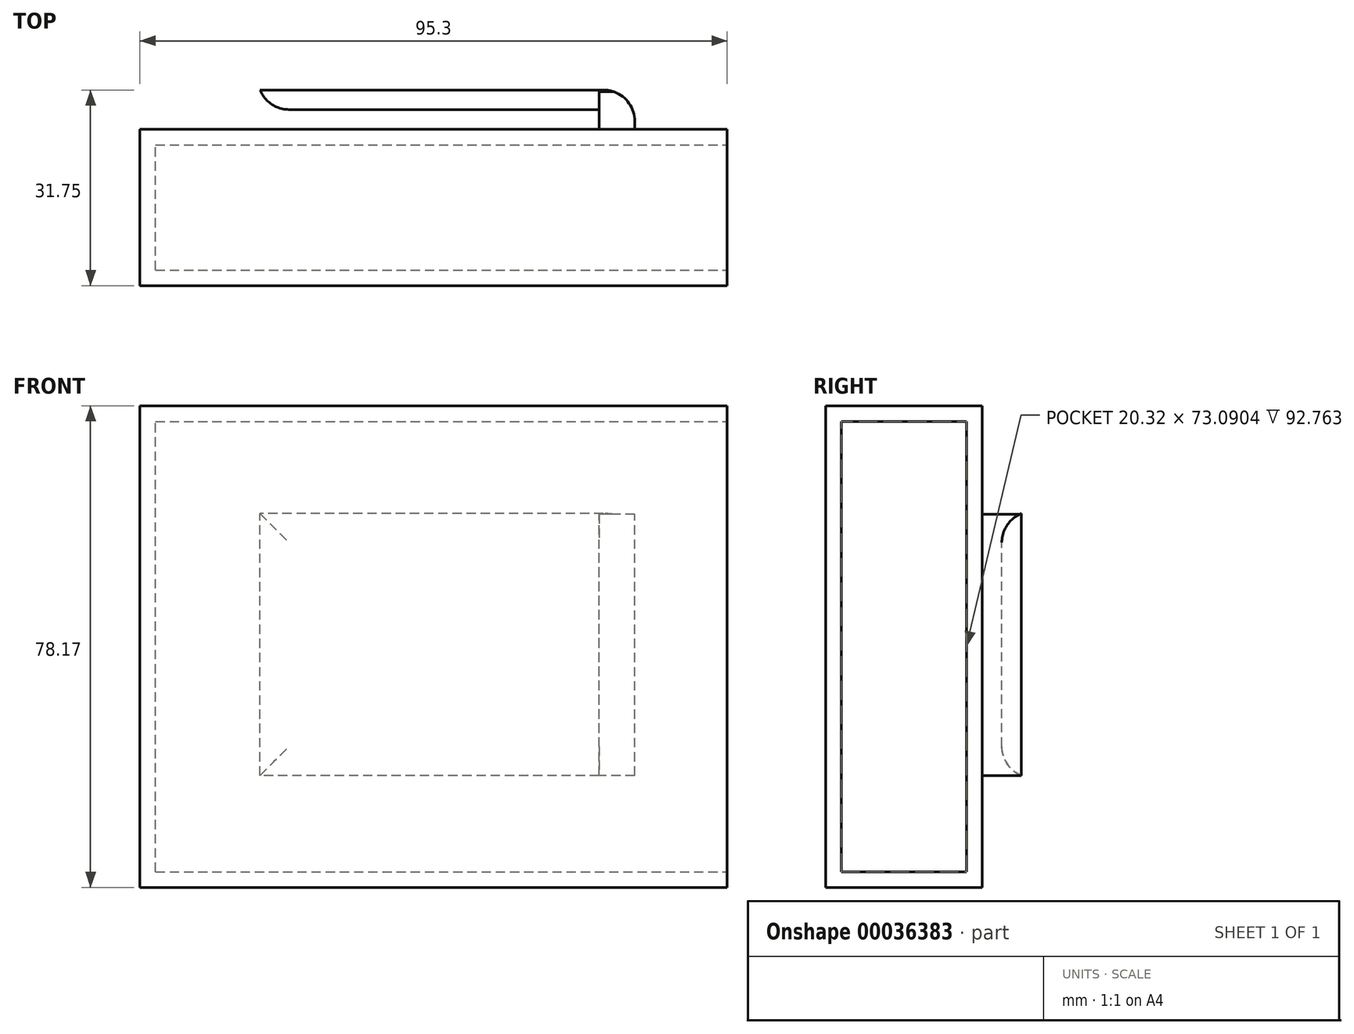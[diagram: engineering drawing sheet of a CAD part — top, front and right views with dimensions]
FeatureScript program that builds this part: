
annotation { "Feature Type Name" : "Feature", "Feature Type Description" : "" }
export const myFeature = defineFeature(function(context is Context, id is Id, definition is map)
    precondition{}
    {
        {
            var Q0;
            Q0=qCreatedBy(makeId("Front.planeOp"),FACE);
            var sketch = newSketch(context, id + "F0", { "sketchPlane" : qUnion([Q0])});
            skLineSegment(sketch, "E0.bottom", {"start": v(0, 0) * mm, "end": v(95.3, 0) * mm});
            skLineSegment(sketch, "E0.top", {"start": v(0, 78.17) * mm, "end": v(95.3, 78.17) * mm});
            skLineSegment(sketch, "E0.left", {"start": v(0, 0) * mm, "end": v(0, 78.17) * mm});
            skLineSegment(sketch, "E0.right", {"start": v(95.3, 0) * mm, "end": v(95.3, 78.17) * mm});
            skSolve(sketch);
        }
        {
            var Q0;
            Q0=makeQuery(id+"F0.imprint","IMPRINT",FACE,{"disambiguationData":[TD([[makeQuery(id+"F0.imprint","IMPRINT",EDGE,{"derivedFrom":sQuery(id+"F0.wireOp",EDGE,"E0.bottom")}),1.0]])]});
            extrude(context, id + "F1", {"entities" : qUnion([Q0]), "depth" : 25.4 * mm});
        }
        {
            var Q0;
            Q0=makeQuery(id+"F1.opExtrude","SWEPT_FACE",FACE,{"disambiguationData":[OSD([sQuery(id+"F0.wireOp",EDGE,"E0.right")])]});
            shell(context, id + "F2", {"entities" : qUnion([Q0]), "thickness" : 2.54 * mm});
        }
        {
            var Q0;
            Q0=makeQuery(id+"F1.opExtrude","CAP_FACE",FACE,{"disambiguationData":[OSD([sQuery(id+"F0.wireOp",EDGE,"E0.bottom"),sQuery(id+"F0.wireOp",EDGE,"E0.top"),sQuery(id+"F0.wireOp",EDGE,"E0.left"),sQuery(id+"F0.wireOp",EDGE,"E0.right")])],"isStart":true});
            var sketch = newSketch(context, id + "F3", { "sketchPlane" : qUnion([Q0])});
            skLineSegment(sketch, "E1.bottom", {"start": v(-80.29, 18.15) * mm, "end": v(-74.51, 18.15) * mm});
            skLineSegment(sketch, "E1.top", {"start": v(-80.29, 60.54) * mm, "end": v(-74.51, 60.54) * mm});
            skLineSegment(sketch, "E1.left", {"start": v(-80.29, 18.15) * mm, "end": v(-80.29, 60.54) * mm});
            skLineSegment(sketch, "E1.right", {"start": v(-74.51, 18.15) * mm, "end": v(-74.51, 60.54) * mm});
            skSolve(sketch);
        }
        {
            var Q0;
            Q0=makeQuery(id+"F3.imprint","IMPRINT",FACE,{"disambiguationData":[TD([[makeQuery(id+"F3.imprint","IMPRINT",EDGE,{"derivedFrom":sQuery(id+"F3.wireOp",EDGE,"E1.bottom")}),1.0]])]});
            extrude(context, id + "F4", {"entities" : qUnion([Q0]), "operationType" : NewBodyOperationType.ADD, "depth" : 3.17 * mm});
        }
        {
            var Q0;
            Q0=makeQuery(id+"F4.opExtrude","CAP_FACE",FACE,{"disambiguationData":[OSD([sQuery(id+"F3.wireOp",EDGE,"E1.bottom"),sQuery(id+"F3.wireOp",EDGE,"E1.top"),sQuery(id+"F3.wireOp",EDGE,"E1.left"),sQuery(id+"F3.wireOp",EDGE,"E1.right")])],"isStart":false});
            var sketch = newSketch(context, id + "F5", { "sketchPlane" : qUnion([Q0])});
            skLineSegment(sketch, "E2.bottom", {"start": v(-80.29, 18.15) * mm, "end": v(-19.47, 18.15) * mm});
            skLineSegment(sketch, "E2.top", {"start": v(-80.29, 60.67) * mm, "end": v(-19.47, 60.67) * mm});
            skLineSegment(sketch, "E2.left", {"start": v(-80.29, 18.15) * mm, "end": v(-80.29, 60.67) * mm});
            skLineSegment(sketch, "E2.right", {"start": v(-19.47, 18.15) * mm, "end": v(-19.47, 60.67) * mm});
            skSolve(sketch);
        }
        {
            var Q0;
            {var subQ4=sQuery(id+"F5.wireOp",EDGE,"E2.top");Q0=makeQuery(id+"F5.imprint","IMPRINT",FACE,{"disambiguationData":[TD([[makeQuery(id+"F5.imprint","IMPRINT",EDGE,{"derivedFrom":subQ4}),-1.0]])]});}
            var Q1;
            {var subQ1=makeQuery(id+"F4.opExtrude","CAP_EDGE",EDGE,{"disambiguationData":[OSD([sQuery(id+"F3.wireOp",EDGE,"E1.top")])],"isStart":false});Q1=makeQuery(id+"F5.imprint","IMPRINT",FACE,{"disambiguationData":[TD([[makeQuery(id+"F5.imprint","IMPRINT",EDGE,{"derivedFrom":subQ1}),-1.0]])]});}
            extrude(context, id + "F6", {"entities" : qUnion([Q0, Q1]), "operationType" : NewBodyOperationType.ADD, "depth" : 3.17 * mm});
        }
        {
            var Q0;
            Q0=makeQuery(id+"F6.opExtrude","CAP_EDGE",EDGE,{"disambiguationData":[OSD([sQuery(id+"F5.wireOp",EDGE,"E2.right")])],"isStart":true});
            var Q1;
            Q1=makeQuery(id+"F6.opExtrude","CAP_EDGE",EDGE,{"disambiguationData":[OSD([sQuery(id+"F5.wireOp",EDGE,"E2.top")])],"isStart":true});
            var Q2;
            Q2=makeQuery(id+"F6.opExtrude","CAP_EDGE",EDGE,{"disambiguationData":[OSD([sQuery(id+"F5.wireOp",EDGE,"E2.bottom")])],"isStart":true});
            fillet(context, id + "F7", {"entities" : qUnion([Q0, Q1, Q2]), "radius" : 5.08 * mm, "tangentPropagation" : true, "allowEdgeOverflow" : false});
        }
        {
            var Q0;
            Q0=makeQuery(id+"F4.opExtrude","CAP_EDGE",EDGE,{"disambiguationData":[OSD([sQuery(id+"F3.wireOp",EDGE,"E1.right")])],"isStart":false});
            var Q1;
            Q1=makeQuery(id+"F6.opExtrude","CAP_EDGE",EDGE,{"disambiguationData":[OSD([sQuery(id+"F5.wireOp",EDGE,"E2.left")])],"isStart":false});
            fillet(context, id + "F8", {"entities" : qUnion([Q0, Q1]), "radius" : 5.08 * mm, "tangentPropagation" : true, "allowEdgeOverflow" : false});
        }
    });
